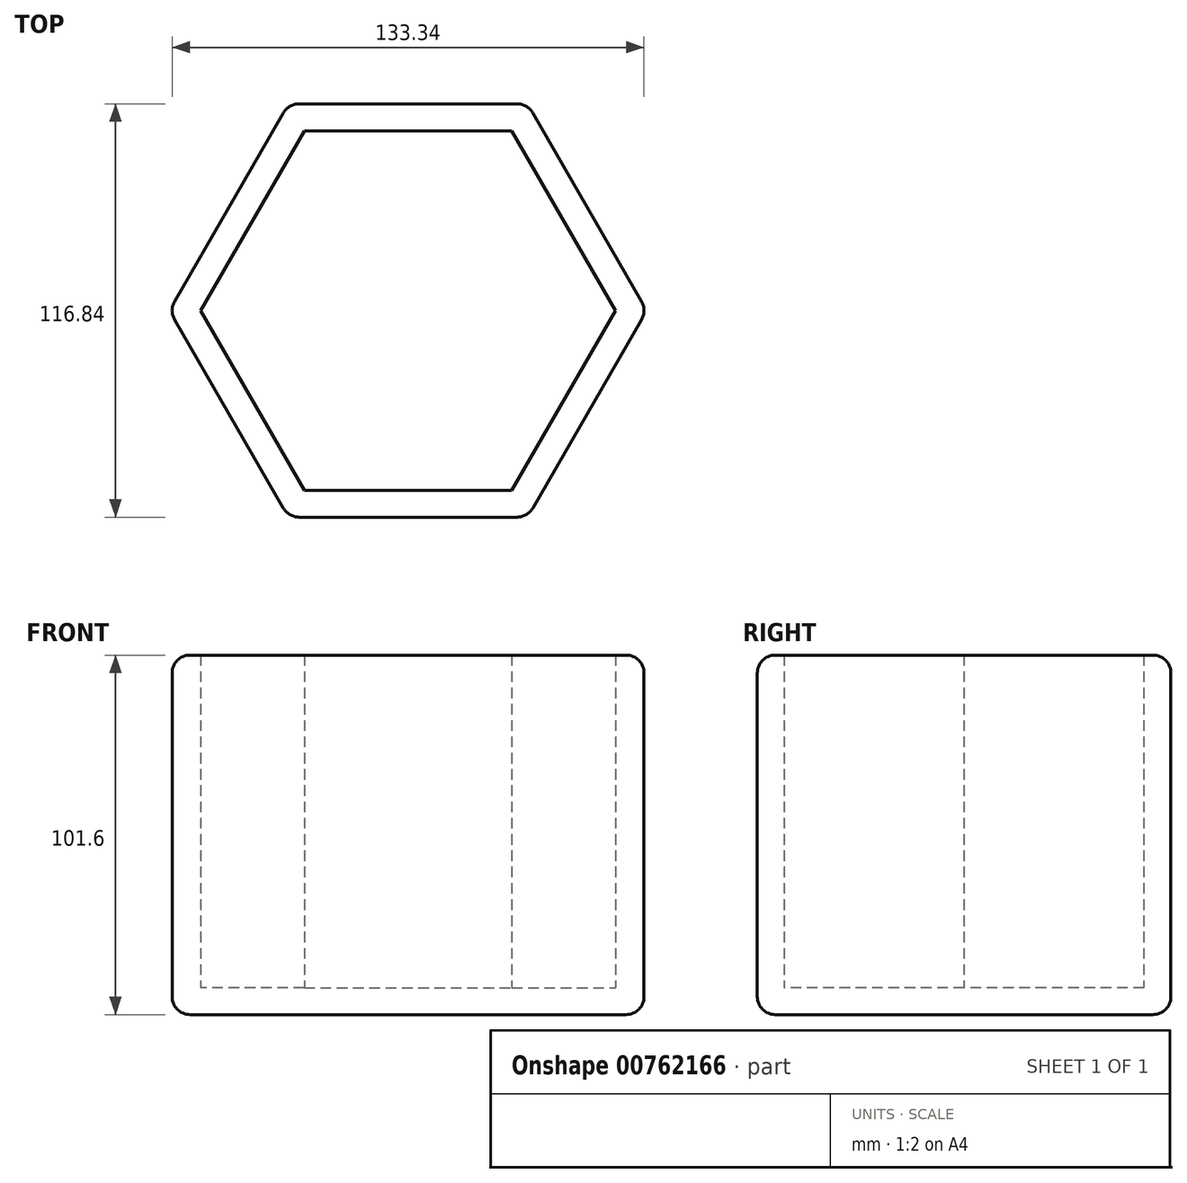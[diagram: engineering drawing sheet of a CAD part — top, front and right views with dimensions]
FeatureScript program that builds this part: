
annotation { "Feature Type Name" : "Feature", "Feature Type Description" : "" }
export const myFeature = defineFeature(function(context is Context, id is Id, definition is map)
    precondition{}
    {
        {
            var Q0;
            Q0=qCreatedBy(makeId("Top.planeOp"),FACE);
            var sketch = newSketch(context, id + "F0", { "sketchPlane" : qUnion([Q0])});
            skLineSegment(sketch, "E0", {"start": v(0, 0) * mm, "end": v(0, 50.8) * mm});
            skLineSegment(sketch, "E1.0", {"start": v(-29.33, 50.8) * mm, "end": v(29.33, 50.8) * mm});
            skLineSegment(sketch, "E1.1", {"start": v(29.33, 50.8) * mm, "end": v(58.66, 0) * mm});
            skLineSegment(sketch, "E1.2", {"start": v(58.66, 0) * mm, "end": v(29.33, -50.8) * mm});
            skLineSegment(sketch, "E1.3", {"start": v(29.33, -50.8) * mm, "end": v(-29.33, -50.8) * mm});
            skLineSegment(sketch, "E1.4", {"start": v(-29.33, -50.8) * mm, "end": v(-58.66, 0) * mm});
            skLineSegment(sketch, "E1.5", {"start": v(-58.66, 0) * mm, "end": v(-29.33, 50.8) * mm});
            skPoint(sketch, "E1.0.midPoint", {"position": v(0, 50.8) * mm});
            skLineSegment(sketch, "E2", {"start": v(0, 0) * mm, "end": v(0, 58.42) * mm});
            skLineSegment(sketch, "E3.0", {"start": v(-33.73, 58.42) * mm, "end": v(33.73, 58.42) * mm});
            skLineSegment(sketch, "E3.1", {"start": v(33.73, 58.42) * mm, "end": v(67.46, 0) * mm});
            skLineSegment(sketch, "E3.2", {"start": v(67.46, 0) * mm, "end": v(33.73, -58.42) * mm});
            skLineSegment(sketch, "E3.3", {"start": v(33.73, -58.42) * mm, "end": v(-33.73, -58.42) * mm});
            skLineSegment(sketch, "E3.4", {"start": v(-33.73, -58.42) * mm, "end": v(-67.46, 0) * mm});
            skLineSegment(sketch, "E3.5", {"start": v(-67.46, 0) * mm, "end": v(-33.73, 58.42) * mm});
            skPoint(sketch, "E3.0.midPoint", {"position": v(0, 58.42) * mm});
            skSolve(sketch);
        }
        {
            var Q0;
            {var subQ7=sQuery(id+"F0.wireOp",EDGE,"E1.1");Q0=makeQuery(id+"F0.imprint","IMPRINT",FACE,{"disambiguationData":[TD([[makeQuery(id+"F0.imprint","IMPRINT",EDGE,{"derivedFrom":subQ7}),1.0]])]});}
            extrude(context, id + "F1", {"entities" : qUnion([Q0]), "depth" : 101.6 * mm, "offsetDistance" : 25.4 * mm});
        }
        {
            var Q0;
            {var subQ0=sQuery(id+"F0.wireOp",EDGE,"E1.1");Q0=makeQuery(id+"F0.imprint","IMPRINT",FACE,{"disambiguationData":[TD([[makeQuery(id+"F0.imprint","IMPRINT",EDGE,{"derivedFrom":subQ0}),-1.0]])]});}
            extrude(context, id + "F2", {"entities" : qUnion([Q0]), "operationType" : NewBodyOperationType.ADD, "depth" : 7.62 * mm, "offsetDistance" : 25.4 * mm});
        }
        {
            var Q0;
            Q0=makeQuery(id+"F1.opExtrude","SWEPT_FACE",FACE,{"disambiguationData":[OSD([sQuery(id+"F0.wireOp",EDGE,"E3.0")])]});
            var Q1;
            Q1=makeQuery(id+"F1.opExtrude","SWEPT_FACE",FACE,{"disambiguationData":[OSD([sQuery(id+"F0.wireOp",EDGE,"E3.5")])]});
            var Q2;
            Q2=makeQuery(id+"F1.opExtrude","SWEPT_FACE",FACE,{"disambiguationData":[OSD([sQuery(id+"F0.wireOp",EDGE,"E3.4")])]});
            var Q3;
            Q3=makeQuery(id+"F1.opExtrude","SWEPT_FACE",FACE,{"disambiguationData":[OSD([sQuery(id+"F0.wireOp",EDGE,"E3.3")])]});
            var Q4;
            Q4=makeQuery(id+"F1.opExtrude","SWEPT_FACE",FACE,{"disambiguationData":[OSD([sQuery(id+"F0.wireOp",EDGE,"E3.1")])]});
            var Q5;
            Q5=makeQuery(id+"F1.opExtrude","SWEPT_FACE",FACE,{"disambiguationData":[OSD([sQuery(id+"F0.wireOp",EDGE,"E3.2")])]});
            fillet(context, id + "F3", {"entities" : qUnion([Q0, Q1, Q2, Q3, Q4, Q5]), "radius" : 5.08 * mm, "tangentPropagation" : true, "allowEdgeOverflow" : false});
        }
    });
